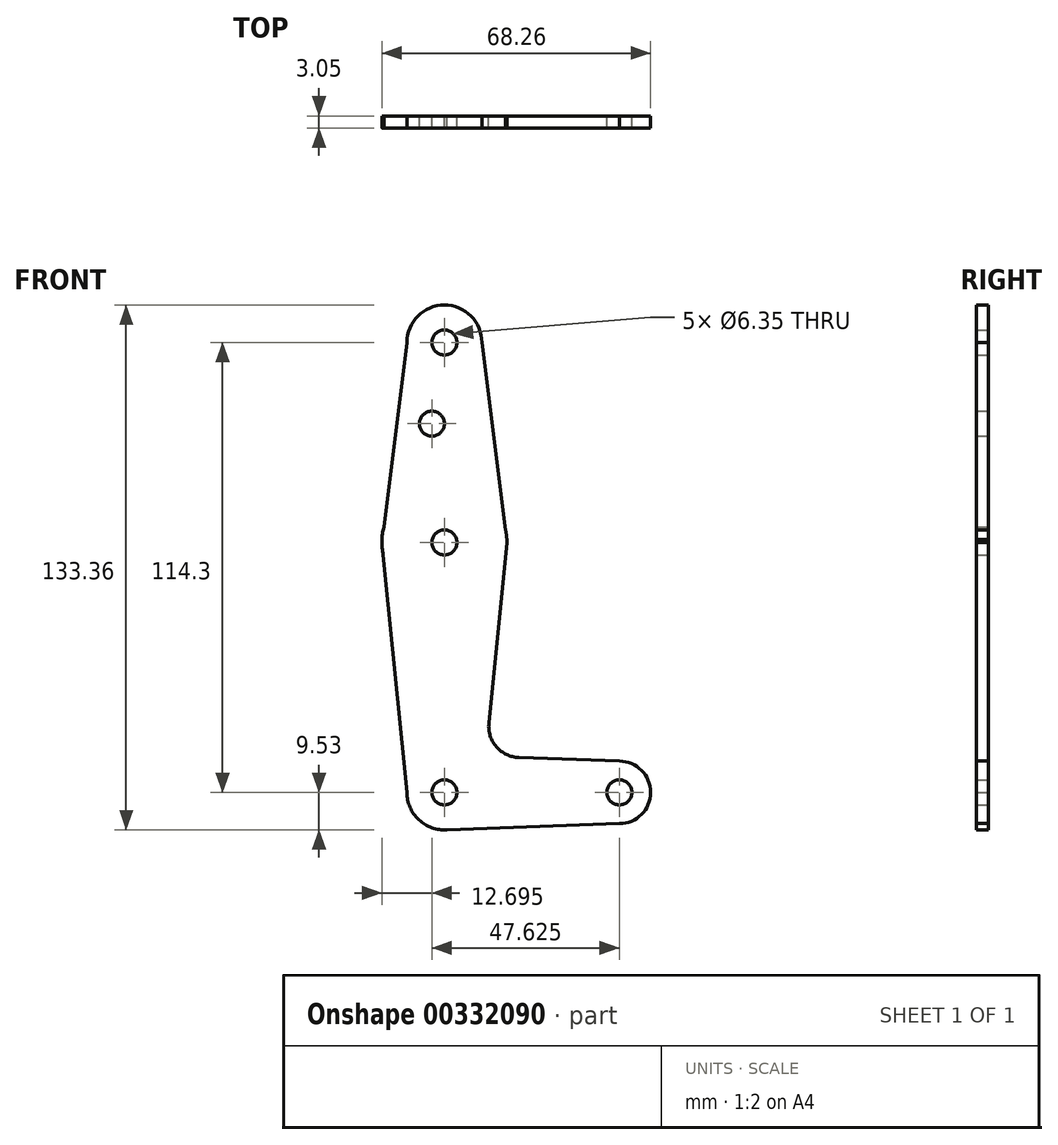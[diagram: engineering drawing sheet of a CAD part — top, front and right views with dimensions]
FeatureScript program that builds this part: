
annotation { "Feature Type Name" : "Feature", "Feature Type Description" : "" }
export const myFeature = defineFeature(function(context is Context, id is Id, definition is map)
    precondition{}
    {
        {
            var Q0;
            Q0=qCreatedBy(makeId("Front.planeOp"),FACE);
            var sketch = newSketch(context, id + "F0", { "sketchPlane" : qUnion([Q0])});
            skLineSegment(sketch, "E0", {"start": v(0, 0) * mm, "end": v(0, 114.3) * mm, "construction": true});
            skLineSegment(sketch, "E1", {"start": v(0, 0) * mm, "end": v(44.45, 0) * mm, "construction": true});
            skCircle(sketch, "E2", {"center": v(0, 0) * mm, "radius": 9.53 * mm});
            skCircle(sketch, "E3", {"center": v(44.45, 0) * mm, "radius": 7.94 * mm});
            skCircle(sketch, "E4", {"center": v(0, 114.3) * mm, "radius": 9.53 * mm});
            skCircle(sketch, "E5", {"center": v(0, 63.5) * mm, "radius": 15.88 * mm});
            skLineSegment(sketch, "E6", {"start": v(-9.53, 114.3) * mm, "end": v(-15.88, 63.5) * mm});
            skLineSegment(sketch, "E7", {"start": v(-15.88, 63.5) * mm, "end": v(-9.52, 0) * mm});
            skLineSegment(sketch, "E8", {"start": v(44.45, 7.94) * mm, "end": v(18.93, 8.85) * mm});
            skLineSegment(sketch, "E9", {"start": v(11.3, 17.6) * mm, "end": v(15.96, 63.5) * mm});
            skLineSegment(sketch, "E10", {"start": v(15.96, 63.5) * mm, "end": v(9.53, 114.3) * mm});
            skLineSegment(sketch, "E11", {"start": v(0, -9.52) * mm, "end": v(44.45, -7.94) * mm});
            skCircle(sketch, "E12", {"center": v(0, 114.3) * mm, "radius": 3.18 * mm});
            skCircle(sketch, "E13", {"center": v(0, 63.5) * mm, "radius": 3.18 * mm});
            skCircle(sketch, "E14", {"center": v(0, 0) * mm, "radius": 3.18 * mm});
            skCircle(sketch, "E15", {"center": v(44.45, 0) * mm, "radius": 3.18 * mm});
            skCircle(sketch, "E16", {"center": v(-3.18, 93.68) * mm, "radius": 3.18 * mm});
            skPoint(sketch, "E17.newPointA", {"position": v(0, 9.53) * mm});
            skPoint(sketch, "E17.newPointB", {"position": v(9.52, 0) * mm});
            skArc(sketch, "E17.filletArc", {"start": v(11.3, 17.6) * mm, "mid": v(13.22, 11.57) * mm, "end": v(18.93, 8.85) * mm});
            skSolve(sketch);
        }
        {
            var Q0;
            Q0 = qSketchRegion(id + "F0", true);
            extrude(context, id + "F1", {"entities" : qUnion([Q0]), "depth" : 3.05 * mm});
        }
    });
